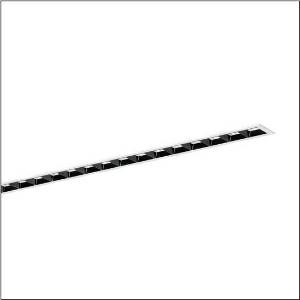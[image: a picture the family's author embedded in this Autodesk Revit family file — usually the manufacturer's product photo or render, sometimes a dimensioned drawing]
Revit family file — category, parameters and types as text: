
# Revit family: silica_r__21_51mx11tat4w_b1e5
name_source: partatom
category: Lighting Fixtures
units: mm (PartAtom-declared; Revit-internal decimal feet)

## family parameters
Cut with Voids When Loaded = No
Host = Face
Light Source = No
Part Type = Normal
Room Calculation Point = No
Round Connector Dimension = Use Diameter
Shared = No

## types (1)
- --- (1 x LED, 3720 lm, 32.2 W, 6500K)
    Apparent Load = 32 VA
    CIE Flux Codes = 85 99 100 100 100
    Color Rendering = 80
    Color Temperature = 6500K
    Default Elevation = 1800 mm
    Description = Silica® 21, office luminaire, primary light control with darklight reflector, of PMMA, black, CAT 2 (L<= 3000cd/m²), light emission: direct distribution, primary light characteristic: symmetric, installation type: recessed, LED, rated luminous flux: 3.720lm, luminous efficacy: 110lm/W, light colour: 8tw, colour temperature: 2700..6500K, control gear: DALI DT8, with terminal, 3+2-pole, max. 2.5mm², mains connection: 220..240V, AC, 50/60Hz, rated input power: 33.8W, luminaire housing, of aluminium, traffic white (RAL 9016), length: 1.228mm, width: 79mm, height: 53mm, protection rating (complete): IP20, insulation class (complete): insulation class I (protective earthing), certification: CE, ENEC, VDE, permissible operating ambient temperature: 0..+35°C, standard: EN 50419, packaging unit: 1 piece
    Height = 0 mm  [stored 0 ft]
    Lamp = 1 x LED
    Lamp Light Flux = 3720 lm
    Lamp Power = 32.2 W
    Lamp count = 1
    Length = 1227 mm
    Luminous efficacy = 116 lm/W
    Manufacturer = Siteco
    ModVariant = No
    Model = 51MX11TAT4W
    Mounting Place = Ceiling
    Mounting Type = Recessed
    Number of Poles = 1
    OnlyDefault = Yes
    Power Factor = 1
    Product Name = Silica® 21
    Product group = office luminaire | ceiling recessed
    ProductGroupID = 401
    Protection Class = Protection class I
    Protection Degree = IP 20
    RLX_Detail_Level = 1
    RLX_Emergency_Light_Flux = 0 lm
    RLX_Emergency_Type = 0
    RLX_Emergency_Type_DB = No
    RlxData = <blob elided: 35529 chars, md5=d79043de>
    Socket = socket
    Standby Power = 0 W
    System Light Flux = 3720 lm
    System Power = 32 W
    Type Comments = individual setting
    Type Image = l_1335880.jpg
    URL = http://relux.com
    VarID = @adj_140106
    Voltage = 0 V
    Weight = 0.00 kg
    Width = 79 mm

note: [stored X ft] marks values corroborated as IEEE doubles in the binary element streams (Revit-internal decimal feet)

## geometry (parser evidence)
native form markers: Blend x4, Sweep x9
no freeform markers — native parametric forms only
